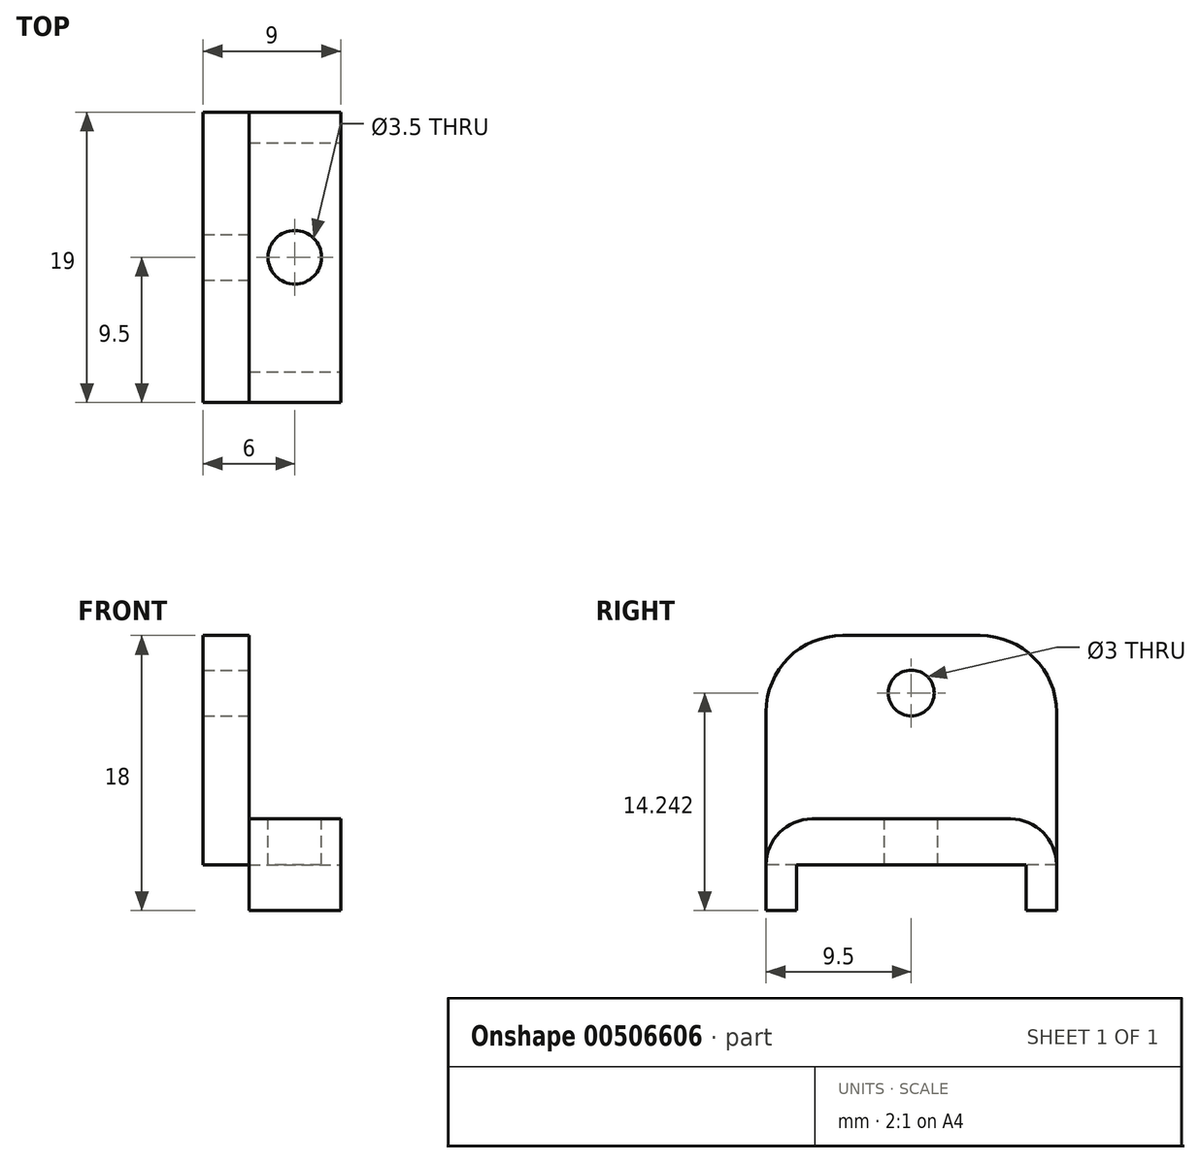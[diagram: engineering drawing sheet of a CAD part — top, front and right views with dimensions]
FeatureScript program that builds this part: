
annotation { "Feature Type Name" : "Feature", "Feature Type Description" : "" }
export const myFeature = defineFeature(function(context is Context, id is Id, definition is map)
    precondition{}
    {
        {
            var Q0;
            Q0=qCreatedBy(makeId("Top.planeOp"),FACE);
            var sketch = newSketch(context, id + "F0", { "sketchPlane" : qUnion([Q0])});
            skLineSegment(sketch, "E0.bottom", {"start": v(0, 9.5) * mm, "end": v(6, 9.5) * mm});
            skLineSegment(sketch, "E0.top", {"start": v(0, -9.5) * mm, "end": v(6, -9.5) * mm});
            skLineSegment(sketch, "E0.left", {"start": v(0, 9.5) * mm, "end": v(0, -9.5) * mm});
            skLineSegment(sketch, "E0.right", {"start": v(6, 9.5) * mm, "end": v(6, -9.5) * mm});
            skSolve(sketch);
        }
        {
            var Q0;
            Q0=makeQuery(id+"F0.imprint","IMPRINT",FACE,{"disambiguationData":[TD([[makeQuery(id+"F0.imprint","IMPRINT",EDGE,{"derivedFrom":sQuery(id+"F0.wireOp",EDGE,"E0.bottom")}),-1.0]])]});
            extrude(context, id + "F1", {"entities" : qUnion([Q0]), "depth" : 3 * mm});
        }
        {
            var Q0;
            Q0=makeQuery(id+"F1.opExtrude","CAP_FACE",FACE,{"disambiguationData":[OSD([sQuery(id+"F0.wireOp",EDGE,"E0.bottom"),sQuery(id+"F0.wireOp",EDGE,"E0.top"),sQuery(id+"F0.wireOp",EDGE,"E0.left"),sQuery(id+"F0.wireOp",EDGE,"E0.right")])],"isStart":true});
            var sketch = newSketch(context, id + "F2", { "sketchPlane" : qUnion([Q0])});
            skLineSegment(sketch, "E1.bottom", {"start": v(0, 9.5) * mm, "end": v(6, 9.5) * mm});
            skLineSegment(sketch, "E1.top", {"start": v(0, 7.5) * mm, "end": v(6, 7.5) * mm});
            skLineSegment(sketch, "E1.left", {"start": v(0, 9.5) * mm, "end": v(0, 7.5) * mm});
            skLineSegment(sketch, "E1.right", {"start": v(6, 9.5) * mm, "end": v(6, 7.5) * mm});
            skLineSegment(sketch, "E2.bottom", {"start": v(0, -9.5) * mm, "end": v(6, -9.5) * mm});
            skLineSegment(sketch, "E2.top", {"start": v(0, -7.5) * mm, "end": v(6, -7.5) * mm});
            skLineSegment(sketch, "E2.left", {"start": v(0, -9.5) * mm, "end": v(0, -7.5) * mm});
            skLineSegment(sketch, "E2.right", {"start": v(6, -9.5) * mm, "end": v(6, -7.5) * mm});
            skSolve(sketch);
        }
        {
            var Q0;
            Q0=makeQuery(id+"F2.imprint","IMPRINT",FACE,{"disambiguationData":[TD([[makeQuery(id+"F2.imprint","IMPRINT",EDGE,{"derivedFrom":sQuery(id+"F2.wireOp",EDGE,"E1.bottom")}),-1.0]])]});
            var Q1;
            Q1=makeQuery(id+"F2.imprint","IMPRINT",FACE,{"disambiguationData":[TD([[makeQuery(id+"F2.imprint","IMPRINT",EDGE,{"derivedFrom":sQuery(id+"F2.wireOp",EDGE,"E2.bottom")}),1.0]])]});
            extrude(context, id + "F3", {"entities" : qUnion([Q0, Q1]), "operationType" : NewBodyOperationType.ADD, "depth" : 3 * mm});
        }
        {
            var Q0;
            Q0=makeQuery(id+"F1.opExtrude","CAP_FACE",FACE,{"disambiguationData":[OSD([sQuery(id+"F0.wireOp",EDGE,"E0.bottom"),sQuery(id+"F0.wireOp",EDGE,"E0.top"),sQuery(id+"F0.wireOp",EDGE,"E0.left"),sQuery(id+"F0.wireOp",EDGE,"E0.right")])],"isStart":false});
            var sketch = newSketch(context, id + "F4", { "sketchPlane" : qUnion([Q0])});
            skCircle(sketch, "E3", {"center": v(3, 0) * mm, "radius": 1.75 * mm});
            skSolve(sketch);
        }
        {
            var Q0;
            Q0=makeQuery(id+"F4.imprint","IMPRINT",FACE,{"disambiguationData":[TD([[makeQuery(id+"F4.imprint","IMPRINT",EDGE,{"derivedFrom":sQuery(id+"F4.wireOp",EDGE,"E3")}),1.0]])]});
            extrude(context, id + "F5", {"entities" : qUnion([Q0]), "operationType" : NewBodyOperationType.REMOVE, "oppositeDirection" : true, "depth" : 3 * mm});
        }
        {
            var Q0;
            Q0=makeQuery(id+"F3.boolean.opBoolean","MERGE",FACE,{"derivedFrom":[makeQuery(id+"F1.opExtrude","SWEPT_FACE",FACE,{"disambiguationData":[OSD([sQuery(id+"F0.wireOp",EDGE,"E0.left")])]}),makeQuery(id+"F3.opExtrude","SWEPT_FACE",FACE,{"disambiguationData":[OSD([sQuery(id+"F2.wireOp",EDGE,"E1.left")])]}),makeQuery(id+"F3.opExtrude","SWEPT_FACE",FACE,{"disambiguationData":[OSD([sQuery(id+"F2.wireOp",EDGE,"E2.left")])]})]});
            var sketch = newSketch(context, id + "F6", { "sketchPlane" : qUnion([Q0])});
            skPoint(sketch, "E4.oppositeSnap0", {"position": v(-9.5, 0) * mm});
            skLineSegment(sketch, "E4.left", {"start": v(-9.5, 0) * mm, "end": v(-9.5, 0) * mm});
            skLineSegment(sketch, "E5.bottom", {"start": v(-9.5, 0) * mm, "end": v(9.5, 0) * mm});
            skLineSegment(sketch, "E5.top", {"start": v(-9.5, 15) * mm, "end": v(9.5, 15) * mm});
            skLineSegment(sketch, "E5.left", {"start": v(-9.5, 0) * mm, "end": v(-9.5, 15) * mm});
            skLineSegment(sketch, "E5.right", {"start": v(9.5, 0) * mm, "end": v(9.5, 15) * mm});
            skSolve(sketch);
        }
        {
            var Q0;
            {var subQ0=sQuery(id+"F6.wireOp",EDGE,"E5.top");Q0=makeQuery(id+"F6.imprint","IMPRINT",FACE,{"disambiguationData":[TD([[makeQuery(id+"F6.imprint","IMPRINT",EDGE,{"derivedFrom":subQ0}),-1.0]])]});}
            var Q1;
            {var subQ2=sQuery(id+"F0.wireOp",EDGE,"E0.left");var subQ9=makeQuery(id+"F1.opExtrude","CAP_EDGE",EDGE,{"disambiguationData":[OSD([subQ2])],"isStart":false});Q1=makeQuery(id+"F6.imprint","IMPRINT",FACE,{"disambiguationData":[TD([[makeQuery(id+"F6.imprint","IMPRINT",EDGE,{"derivedFrom":subQ9}),-1.0]])]});}
            extrude(context, id + "F7", {"entities" : qUnion([Q0, Q1]), "operationType" : NewBodyOperationType.ADD, "depth" : 3 * mm});
        }
        {
            var Q0;
            Q0=makeQuery(id+"F7.opExtrude","CAP_FACE",FACE,{"disambiguationData":[OSD([sQuery(id+"F6.wireOp",EDGE,"E5.bottom"),sQuery(id+"F6.wireOp",EDGE,"E5.top"),sQuery(id+"F6.wireOp",EDGE,"E5.left"),sQuery(id+"F6.wireOp",EDGE,"E5.right")])],"isStart":true});
            var sketch = newSketch(context, id + "F8", { "sketchPlane" : qUnion([Q0])});
            skCircle(sketch, "E6", {"center": v(0, 11.24) * mm, "radius": 1.5 * mm});
            skSolve(sketch);
        }
        {
            var Q0;
            Q0=makeQuery(id+"F8.imprint","IMPRINT",FACE,{"disambiguationData":[TD([[makeQuery(id+"F8.imprint","IMPRINT",EDGE,{"derivedFrom":sQuery(id+"F8.wireOp",EDGE,"E6")}),1.0]])]});
            extrude(context, id + "F9", {"entities" : qUnion([Q0]), "operationType" : NewBodyOperationType.REMOVE, "oppositeDirection" : true, "depth" : 3 * mm});
        }
        {
            var Q0;
            Q0=makeQuery(id+"F7.opExtrude","SWEPT_EDGE",EDGE,{"disambiguationData":[OSD([sQuery(id+"F6.wireOp",EDGE,"E5.top"),sQuery(id+"F6.wireOp",EDGE,"E5.right")])]});
            var Q1;
            Q1=makeQuery(id+"F7.opExtrude","SWEPT_EDGE",EDGE,{"disambiguationData":[OSD([sQuery(id+"F6.wireOp",EDGE,"E5.top"),sQuery(id+"F6.wireOp",EDGE,"E5.left")])]});
            fillet(context, id + "F10", {"entities" : qUnion([Q0, Q1]), "radius" : 5 * mm, "tangentPropagation" : true, "allowEdgeOverflow" : false});
        }
        {
            var Q0;
            Q0=makeQuery(id+"F1.opExtrude","CAP_EDGE",EDGE,{"disambiguationData":[OSD([sQuery(id+"F0.wireOp",EDGE,"E0.top")])],"isStart":false});
            var Q1;
            Q1=makeQuery(id+"F1.opExtrude","CAP_EDGE",EDGE,{"disambiguationData":[OSD([sQuery(id+"F0.wireOp",EDGE,"E0.bottom")])],"isStart":false});
            fillet(context, id + "F11", {"entities" : qUnion([Q0, Q1]), "radius" : 3 * mm, "tangentPropagation" : true, "allowEdgeOverflow" : false});
        }
    });
